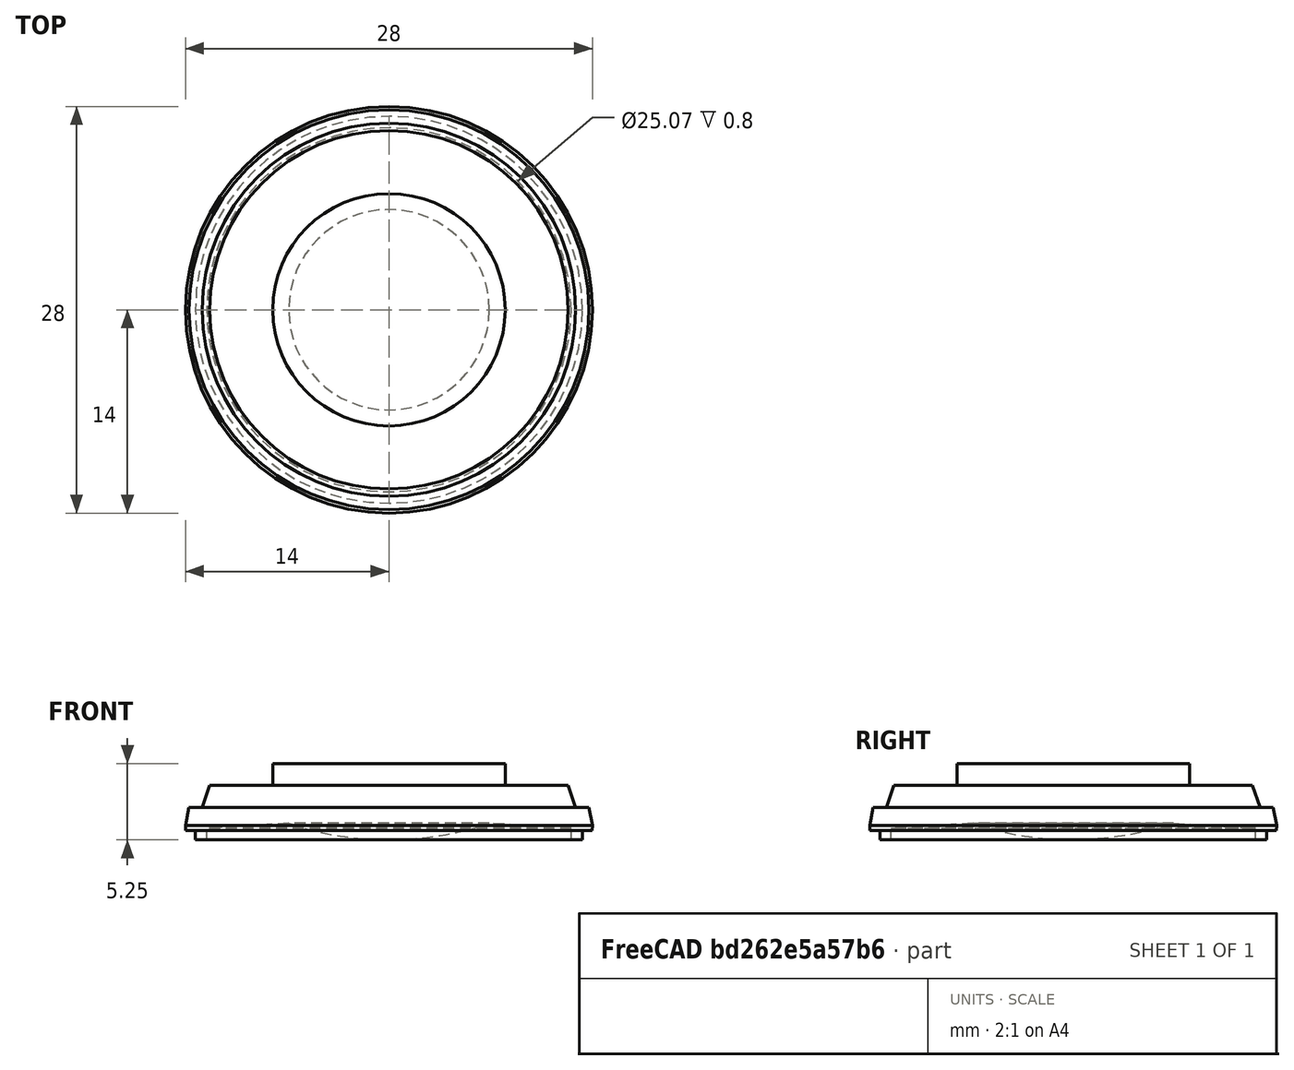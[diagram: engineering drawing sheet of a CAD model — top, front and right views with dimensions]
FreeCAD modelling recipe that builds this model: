
FCSTD DOCUMENT  (FreeCAD 1.0R39109 (Git))
Label: Speaker2W
License: All rights reserved
LicenseURL: http://en.wikipedia.org/wiki/All_rights_reserved
objects: TechDraw::DrawViewDimension×9, TechDraw::DrawProjGroupItem×2, Sketcher::SketchObject×1, PartDesign::Revolution×1, PartDesign::Body×1, TechDraw::DrawSVGTemplate×1, TechDraw::DrawProjGroup×1, TechDraw::DrawPage×1
note: 6 computed .brp shape members not serialized (recipe doc carries the construction recipe); baked Part::Feature solids carry a one-line shape summary decoded from their .brp

FEATURE [Sketcher::SketchObject] Sketch
  ArcFitTolerance = 0
  AttachmentSupport = -> [XZ_Plane]
  FullyConstrained = false
  MakeInternals = false
  MapMode = 5
  Placement = pos=(0,0,0) rot=(1,0,0;1.5708rad)
  sketch-geometry (14):
    g0: LineSegment StartX=0 StartY=5.25 StartZ=0 EndX=8 EndY=5.25 EndZ=0
    g1: LineSegment StartX=8 StartY=5.25 StartZ=0 EndX=8 EndY=3.75 EndZ=0
    g2: LineSegment StartX=8 StartY=3.75 StartZ=0 EndX=12.34 EndY=3.75 EndZ=0
    g3: LineSegment StartX=12.34 StartY=3.75 StartZ=0 EndX=12.85 EndY=2.24 EndZ=0
    g4: LineSegment StartX=12.85 StartY=2.24 StartZ=0 EndX=13.7607 EndY=2.24 EndZ=0
    g5: LineSegment StartX=13.7607 StartY=2.24 StartZ=0 EndX=14 EndY=1 EndZ=0
    g6: LineSegment StartX=14 StartY=1 StartZ=0 EndX=13.99 EndY=0.648005 EndZ=0
    g7: LineSegment StartX=13.99 StartY=0.648005 StartZ=0 EndX=13.315 EndY=0.65 EndZ=0
    g8: LineSegment StartX=13.315 StartY=0.65 StartZ=0 EndX=13.315 EndY=0 EndZ=0
    g9: LineSegment StartX=13.315 StartY=0 StartZ=0 EndX=12.535 EndY=0 EndZ=0
    g10: LineSegment StartX=12.535 StartY=0 StartZ=0 EndX=12.535 EndY=0.8 EndZ=0
    g11: LineSegment StartX=12.535 StartY=0.8 StartZ=0 EndX=6.9 EndY=1.13724 EndZ=0
    g12: LineSegment StartX=9e-16 StartY=0 StartZ=0 EndX=0 EndY=5.25 EndZ=0
    g13: ArcOfCircle CenterX=4.94924e-05 CenterY=21.5006 CenterZ=0 NormalX=0 NormalY=0 NormalZ=1 AngleXU=0 Radius=21.5006 StartAngle=4.71239 EndAngle=5.03909
  constraints (35):
    c: PointOnObject(g0,g-2)
    c: Horizontal(g0)
    c: Coincident(g0,g1)
    c: Vertical(g1)
    c: Coincident(g1,g2)
    c: Coincident(g2,g3)
    c: Coincident(g3,g4)
    c: Coincident(g4,g5)
    c: Coincident(g5,g6)
    c: Coincident(g6,g7)
    c: Coincident(g7,g8)
    c: PointOnObject(g8,g-1)
    c: Vertical(g8)
    c: Coincident(g8,g9)
    c: PointOnObject(g9,g-1)
    c: Coincident(g9,g10)
    c: Coincident(g10,g11)
    c: Coincident(g12,g0)
    c: DistanceX(g0,g0) = 8
    c: DistanceY(g12,g12) = 5.25
    c: DistanceX(g-1,g8) = 13.315
    c: DistanceX(g-1,g6) = 13.99
    c: DistanceY(g8,g8) = 0.65
    c: DistanceY(g-1,g1) = 3.75
    c: DistanceX(g-1,g2) = 12.34
    c: Horizontal(g2,g1)
    c: DistanceX(g9,g8) = 0.78
    c: DistanceX(g-1,g11) = 6.9
    c: DistanceX(g-1,g3) = 12.85
    c: Vertical(g9,g10)
    c: DistanceY(g10,g10) = 0.8
    c: DistanceY(g-1,g3) = 2.24
    c: Horizontal(g3,g4)
    c: Coincident(g13,g11)
    c: Tangent(g13,g-1)
FEATURE [PartDesign::Revolution] Revolution
  Angle = 360
  Angle2 = 60
  Axis = (0,2e-16,1)
  Base = (0,0,0)
  Placement = pos=(0,0,0) rot=(1,0,0;1.5708rad)
  Profile = -> Sketch
  ReferenceAxis = -> Sketch [V_Axis]
  Reversed = true
  Suppressed = false
  Type = 0
FEATURE [PartDesign::Body] Body  label="SpeakerOutline"
  AllowCompound = false
  Group = -> [Sketch,Revolution]
  Origin = -> Origin
  Tip = -> Revolution
FEATURE [TechDraw::DrawSVGTemplate] Template
  EditableTexts = Designed_by_Name=Designed by Name; Drawing_number=Drawing number; FC-Date=Date; FC-SC=Scale; FC-SH=Sheet; FC-Title=Title; Subtitle=Subtitle; Weight=Weight
  Height = 210
  Orientation = 1
  Width = 297
FEATURE [TechDraw::DrawProjGroupItem] ProjItem  label="Front"
  CoarseView = false
  Direction = (0,-1,0)
  Focus = 100
  HardHidden = false
  IsoCount = 0
  IsoHidden = false
  IsoVisible = false
  LockPosition = true
  Perspective = false
  Rotation = 0
  RotationVector = (1,0,0)
  Scale = 2
  ScaleType = 2
  ScrubCount = 0
  SeamHidden = false
  SeamVisible = true
  SmoothHidden = false
  SmoothVisible = true
  Source = -> [Body]
  Type = 0
  X = 0
  XDirection = (1,0,0)
  Y = 0
FEATURE [TechDraw::DrawProjGroupItem] ProjItem001  label="Bottom"
  CoarseView = false
  Direction = (0,0,-1)
  Focus = 100
  HardHidden = false
  IsoCount = 0
  IsoHidden = false
  IsoVisible = false
  LockPosition = false
  Perspective = false
  Rotation = 0
  RotationVector = (1,0,0)
  Scale = 2
  ScaleType = 2
  ScrubCount = 0
  SeamHidden = false
  SeamVisible = true
  SmoothHidden = false
  SmoothVisible = true
  Source = -> [Body]
  Type = 5
  X = 0
  XDirection = (1,0,0)
  Y = 48.25
FEATURE [TechDraw::DrawProjGroup] ProjGroup
  Anchor = -> ProjItem
  AutoDistribute = true
  LockPosition = false
  ProjectionType = 0
  Rotation = 0
  Scale = 2
  ScaleType = 2
  Source = -> [Body]
  Views = -> [ProjItem,ProjItem001]
  X = 156.432
  Y = 86.8705
  spacingX = 15
  spacingY = 15
FEATURE [TechDraw::DrawViewDimension] Dimension
  AngleOverride = false
  Arbitrary = false
  ArbitraryTolerances = false
  EqualTolerance = true
  ExtensionAngle = 0
  FormatSpec = ⌀%.3f
  FormatSpecOverTolerance = %+.3f
  FormatSpecUnderTolerance = %+.3f
  Inverted = false
  LineAngle = 0
  LockPosition = false
  MeasureType = 1
  OverTolerance = 0
  References2D = -> [ProjItem001]
  Rotation = 0
  Scale = 2
  ScaleType = 2
  TheoreticalExact = false
  Type = 5
  UnderTolerance = 0
  X = -47.2361
  Y = 24.8248
FEATURE [TechDraw::DrawViewDimension] Dimension001
  AngleOverride = false
  Arbitrary = false
  ArbitraryTolerances = false
  EqualTolerance = true
  ExtensionAngle = 0
  FormatSpec = ⌀%.3f
  FormatSpecOverTolerance = %+.3f
  FormatSpecUnderTolerance = %+.3f
  Inverted = false
  LineAngle = 0
  LockPosition = false
  MeasureType = 1
  OverTolerance = 0
  References2D = -> [ProjItem001]
  Rotation = 0
  Scale = 2
  ScaleType = 2
  TheoreticalExact = false
  Type = 5
  UnderTolerance = 0
  X = -48.2705
  Y = 11.378
FEATURE [TechDraw::DrawViewDimension] Dimension002
  AngleOverride = false
  Arbitrary = false
  ArbitraryTolerances = false
  EqualTolerance = true
  ExtensionAngle = 0
  FormatSpec = ⌀%.3f
  FormatSpecOverTolerance = %+.3f
  FormatSpecUnderTolerance = %+.3f
  Inverted = false
  LineAngle = 0
  LockPosition = false
  MeasureType = 1
  OverTolerance = 0
  References2D = -> [ProjItem001]
  Rotation = 0
  Scale = 2
  ScaleType = 2
  TheoreticalExact = false
  Type = 5
  UnderTolerance = 0
  X = -49.3049
  Y = -2.06874
FEATURE [TechDraw::DrawViewDimension] Dimension003
  AngleOverride = false
  Arbitrary = false
  ArbitraryTolerances = false
  EqualTolerance = true
  ExtensionAngle = 0
  FormatSpec = ⌀%.3f
  FormatSpecOverTolerance = %+.3f
  FormatSpecUnderTolerance = %+.3f
  Inverted = false
  LineAngle = 0
  LockPosition = false
  MeasureType = 1
  OverTolerance = 0
  References2D = -> [ProjItem001]
  Rotation = 0
  Scale = 2
  ScaleType = 2
  TheoreticalExact = false
  Type = 5
  UnderTolerance = 0
  X = -47.8874
  Y = -17.9578
FEATURE [TechDraw::DrawViewDimension] Dimension004
  AngleOverride = false
  Arbitrary = false
  ArbitraryTolerances = false
  EqualTolerance = true
  ExtensionAngle = 0
  FormatSpec = %.3f
  FormatSpecOverTolerance = %+.3f
  FormatSpecUnderTolerance = %+.3f
  Inverted = false
  LineAngle = 0
  LockPosition = false
  MeasureType = 1
  OverTolerance = 0
  References2D = -> [ProjItem]
  Rotation = 0
  Scale = 2
  ScaleType = 2
  TheoreticalExact = false
  Type = 2
  UnderTolerance = 0
  X = 45.9417
  Y = -11.6364
FEATURE [TechDraw::DrawViewDimension] Dimension005
  AngleOverride = false
  Arbitrary = false
  ArbitraryTolerances = false
  EqualTolerance = true
  ExtensionAngle = 0
  FormatSpec = %.3f
  FormatSpecOverTolerance = %+.3f
  FormatSpecUnderTolerance = %+.3f
  Inverted = false
  LineAngle = 0
  LockPosition = false
  MeasureType = 1
  OverTolerance = 0
  References2D = -> [ProjItem]
  Rotation = 0
  Scale = 2
  ScaleType = 2
  TheoreticalExact = false
  Type = 2
  UnderTolerance = 0
  X = 61.9846
  Y = -11.0595
FEATURE [TechDraw::DrawViewDimension] Dimension006
  AngleOverride = false
  Arbitrary = false
  ArbitraryTolerances = false
  EqualTolerance = true
  ExtensionAngle = 0
  FormatSpec = %.3f
  FormatSpecOverTolerance = %+.3f
  FormatSpecUnderTolerance = %+.3f
  Inverted = false
  LineAngle = 0
  LockPosition = false
  MeasureType = 1
  OverTolerance = 0
  References2D = -> [ProjItem]
  Rotation = 0
  Scale = 2
  ScaleType = 2
  TheoreticalExact = false
  Type = 2
  UnderTolerance = 0
  X = 74.8799
  Y = -12.4785
FEATURE [TechDraw::DrawViewDimension] Dimension007
  AngleOverride = false
  Arbitrary = false
  ArbitraryTolerances = false
  EqualTolerance = true
  ExtensionAngle = 0
  FormatSpec = %.3f
  FormatSpecOverTolerance = %+.3f
  FormatSpecUnderTolerance = %+.3f
  Inverted = false
  LineAngle = 0
  LockPosition = false
  MeasureType = 1
  OverTolerance = 0
  References2D = -> [ProjItem]
  Rotation = 0
  Scale = 2
  ScaleType = 2
  TheoreticalExact = false
  Type = 2
  UnderTolerance = 0
  X = 86.2764
  Y = -11.8922
FEATURE [TechDraw::DrawViewDimension] Dimension008
  AngleOverride = false
  Arbitrary = false
  ArbitraryTolerances = false
  EqualTolerance = true
  ExtensionAngle = 0
  FormatSpec = %.3f
  FormatSpecOverTolerance = %+.3f
  FormatSpecUnderTolerance = %+.3f
  Inverted = false
  LineAngle = 0
  LockPosition = false
  MeasureType = 1
  OverTolerance = 0
  References2D = -> [ProjItem]
  Rotation = 0
  Scale = 2
  ScaleType = 2
  TheoreticalExact = false
  Type = 2
  UnderTolerance = 0
  X = 98.8399
  Y = -3.19271
FEATURE [TechDraw::DrawPage] Page  label="Speaker2WMech"
  KeepUpdated = true
  NextBalloonIndex = 1
  ProjectionType = 0
  Template = -> Template
  Views = -> [ProjGroup,Dimension,Dimension001,Dimension002,Dimension003,Dimension004,Dimension005,Dimension006,Dimension007,Dimension008]
